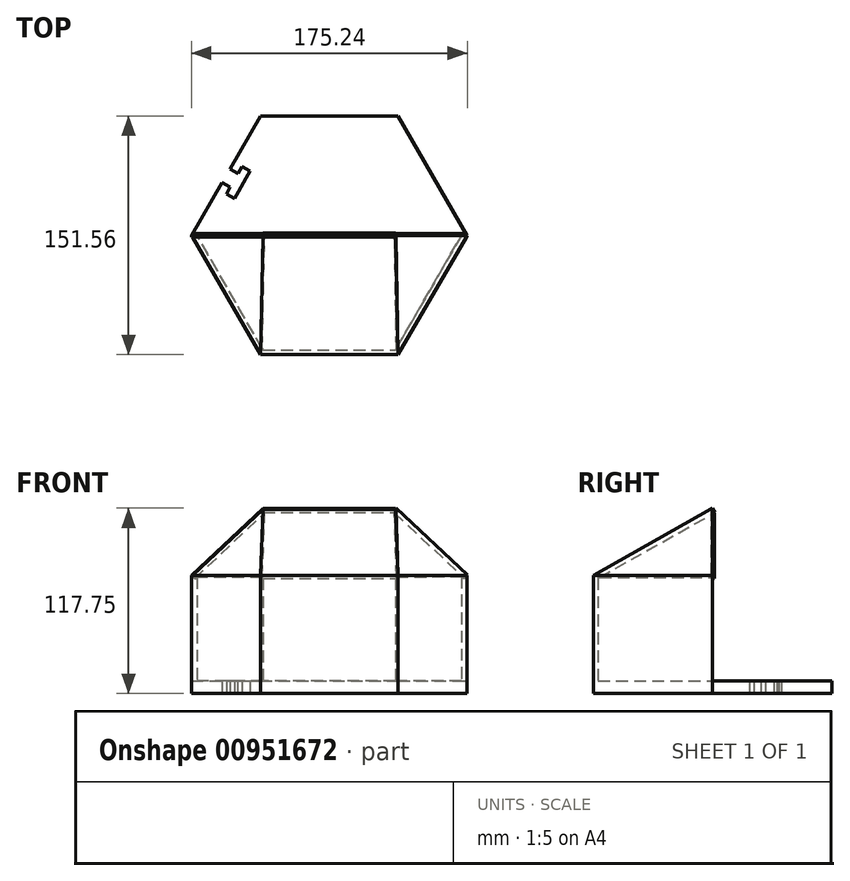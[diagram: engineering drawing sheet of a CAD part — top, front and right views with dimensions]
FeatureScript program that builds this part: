
annotation { "Feature Type Name" : "Feature", "Feature Type Description" : "" }
export const myFeature = defineFeature(function(context is Context, id is Id, definition is map)
    precondition{}
    {
        {
            var Q0;
            Q0=qCreatedBy(makeId("Top.planeOp"),FACE);
            var sketch = newSketch(context, id + "F0", { "sketchPlane" : qUnion([Q0])});
            skCircle(sketch, "E0.cCircle", {"center": v(0, 0) * mm, "radius": 75.78 * mm, "construction": true});
            skLineSegment(sketch, "E0.0", {"start": v(-43.75, 75.78) * mm, "end": v(43.75, 75.78) * mm});
            skLineSegment(sketch, "E0.1", {"start": v(43.75, 75.78) * mm, "end": v(87.5, 0) * mm});
            skLineSegment(sketch, "E0.2", {"start": v(87.5, 0) * mm, "end": v(43.75, -75.78) * mm});
            skLineSegment(sketch, "E0.3", {"start": v(43.75, -75.78) * mm, "end": v(-43.75, -75.78) * mm});
            skLineSegment(sketch, "E0.4", {"start": v(-43.75, -75.78) * mm, "end": v(-87.5, 0) * mm});
            skLineSegment(sketch, "E0.5", {"start": v(-87.5, 0) * mm, "end": v(-43.75, 75.78) * mm});
            skPoint(sketch, "E0.0.midPoint", {"position": v(0, 75.78) * mm});
            skLineSegment(sketch, "E1.0", {"start": v(-84.04, 0) * mm, "end": v(-42.02, 72.78) * mm});
            skLineSegment(sketch, "E1.1", {"start": v(42.02, 72.78) * mm, "end": v(84.04, 0) * mm});
            skLineSegment(sketch, "E1.2", {"start": v(84.04, 0) * mm, "end": v(42.02, -72.78) * mm});
            skLineSegment(sketch, "E1.3", {"start": v(-42.02, 72.78) * mm, "end": v(42.02, 72.78) * mm});
            skLineSegment(sketch, "E1.4", {"start": v(42.02, -72.78) * mm, "end": v(-42.02, -72.78) * mm});
            skLineSegment(sketch, "E1.5", {"start": v(-42.02, -72.78) * mm, "end": v(-84.04, 0) * mm});
            skLineSegment(sketch, "E2", {"start": v(-87.5, 0) * mm, "end": v(-84.04, 0) * mm});
            skLineSegment(sketch, "E3", {"start": v(84.04, 0) * mm, "end": v(87.5, 0) * mm});
            skLineSegment(sketch, "E4", {"start": v(0, 0) * mm, "end": v(0, 72.78) * mm, "construction": true});
            skLineSegment(sketch, "E5", {"start": v(0, 0) * mm, "end": v(42.02, 72.78) * mm, "construction": true});
            skLineSegment(sketch, "E6", {"start": v(0, 0) * mm, "end": v(-42.02, 72.78) * mm, "construction": true});
            skLineSegment(sketch, "E7", {"start": v(0, 36.39) * mm, "end": v(0, 72.78) * mm, "construction": true});
            skLineSegment(sketch, "E8.bottom", {"start": v(25, 48.33) * mm, "end": v(-25, 48.33) * mm});
            skLineSegment(sketch, "E8.top", {"start": v(25, 60.83) * mm, "end": v(-25, 60.83) * mm});
            skLineSegment(sketch, "E8.left", {"start": v(25, 48.33) * mm, "end": v(25, 60.83) * mm});
            skLineSegment(sketch, "E8.right", {"start": v(-25, 48.33) * mm, "end": v(-25, 60.83) * mm});
            skPoint(sketch, "E8.middle", {"position": v(0, 54.58) * mm});
            skLineSegment(sketch, "E9", {"start": v(-65.63, 37.89) * mm, "end": v(-55.16, 32) * mm, "construction": true});
            skLineSegment(sketch, "E10", {"start": v(-55.16, 32) * mm, "end": v(-52.71, 36.37) * mm, "construction": true});
            skLineSegment(sketch, "E11", {"start": v(-55.16, 32) * mm, "end": v(-57.62, 27.65) * mm, "construction": true});
            skLineSegment(sketch, "E12", {"start": v(-52.71, 36.37) * mm, "end": v(-63.12, 42.22) * mm});
            skLineSegment(sketch, "E13", {"start": v(-57.62, 27.65) * mm, "end": v(-52.71, 36.37) * mm});
            skLineSegment(sketch, "E14", {"start": v(-65.63, 37.89) * mm, "end": v(-68.13, 33.56) * mm});
            skLineSegment(sketch, "E15", {"start": v(-57.62, 27.65) * mm, "end": v(-68.13, 33.56) * mm});
            skLineSegment(sketch, "E16.MirrorCS", {"start": v(87.5, 0) * mm, "end": v(43.75, 75.78) * mm});
            skLineSegment(sketch, "E17", {"start": v(-62.87, 30.6) * mm, "end": v(-65.32, 26.25) * mm});
            skLineSegment(sketch, "E18", {"start": v(-57.62, 27.65) * mm, "end": v(-60.07, 23.3) * mm});
            skLineSegment(sketch, "E19", {"start": v(-65.32, 26.25) * mm, "end": v(-60.07, 23.3) * mm});
            skLineSegment(sketch, "E20.MirrorCS", {"start": v(-52.71, 36.37) * mm, "end": v(-50.26, 40.72) * mm});
            skLineSegment(sketch, "E21.MirrorCS", {"start": v(-57.97, 39.32) * mm, "end": v(-55.52, 43.68) * mm});
            skLineSegment(sketch, "E22.MirrorCS", {"start": v(-55.52, 43.68) * mm, "end": v(-50.26, 40.72) * mm});
            skLineSegment(sketch, "E23", {"start": v(-68.13, 33.56) * mm, "end": v(-65.5, 32.09) * mm});
            skSolve(sketch);
        }
        {
            var Q0;
            Q0=makeQuery(id+"F0.imprint","IMPRINT",FACE,{"disambiguationData":[TD([[makeQuery(id+"F0.imprint","IMPRINT",EDGE,{"derivedFrom":sQuery(id+"F0.wireOp",EDGE,"E1.0")}),-1.0]])]});
            extrude(context, id + "F1", {"entities" : qUnion([Q0]), "depth" : 8 * mm, "offsetDistance" : 25 * mm});
        }
        {
            var Q0;
            Q0=makeQuery(id+"F0.imprint","IMPRINT",FACE,{"disambiguationData":[TD([[makeQuery(id+"F0.imprint","IMPRINT",EDGE,{"derivedFrom":sQuery(id+"F0.wireOp",EDGE,"E0.2")}),-1.0]])]});
            extrude(context, id + "F2", {"entities" : qUnion([Q0]), "operationType" : NewBodyOperationType.ADD, "depth" : 75 * mm, "offsetDistance" : 25 * mm});
        }
        {
            var Q0;
            Q0=qCreatedBy(makeId("Front.planeOp"),FACE);
            var sketch = newSketch(context, id + "F3", { "sketchPlane" : qUnion([Q0])});
            skLineSegment(sketch, "E24", {"start": v(0, 0) * mm, "end": v(0, 144.27) * mm, "construction": true});
            skLineSegment(sketch, "E25", {"start": v(0, 144.27) * mm, "end": v(-94, 144.27) * mm, "construction": true});
            skLineSegment(sketch, "E26", {"start": v(0, 144.27) * mm, "end": v(81.74, 144.27) * mm});
            skLineSegment(sketch, "E27", {"start": v(0, 0) * mm, "end": v(0, 75) * mm, "construction": true});
            skLineSegment(sketch, "E28", {"start": v(0, 75) * mm, "end": v(0, 114.5) * mm, "construction": true});
            skLineSegment(sketch, "E29", {"start": v(0, 75) * mm, "end": v(-87.5, 75) * mm, "construction": true});
            skLineSegment(sketch, "E30", {"start": v(0, 114.5) * mm, "end": v(42.02, 114.5) * mm, "construction": true});
            skLineSegment(sketch, "E31", {"start": v(0, 114.5) * mm, "end": v(-42.02, 114.5) * mm});
            skLineSegment(sketch, "E32", {"start": v(0, 75) * mm, "end": v(-84.04, 75) * mm, "construction": true});
            skLineSegment(sketch, "E33", {"start": v(-42.02, 114.5) * mm, "end": v(-84.04, 75) * mm});
            skLineSegment(sketch, "E34", {"start": v(-42.02, 114.5) * mm, "end": v(-42.02, 117.5) * mm, "construction": true});
            skLineSegment(sketch, "E35", {"start": v(-42.02, 117.5) * mm, "end": v(-87.5, 75) * mm});
            skLineSegment(sketch, "E36", {"start": v(-42.02, 117.5) * mm, "end": v(0, 117.5) * mm});
            skLineSegment(sketch, "E37.MirrorCS", {"start": v(42.02, 117.5) * mm, "end": v(87.5, 75) * mm});
            skLineSegment(sketch, "E38.MirrorCS", {"start": v(42.02, 114.5) * mm, "end": v(84.04, 75) * mm});
            skLineSegment(sketch, "E39.MirrorCS", {"start": v(42.02, 117.5) * mm, "end": v(0, 117.5) * mm});
            skLineSegment(sketch, "E40.MirrorCS", {"start": v(0, 114.5) * mm, "end": v(42.02, 114.5) * mm});
            skLineSegment(sketch, "E41", {"start": v(87.5, 75) * mm, "end": v(84.04, 75) * mm});
            skLineSegment(sketch, "E42", {"start": v(-84.04, 75) * mm, "end": v(-87.5, 75) * mm});
            skSolve(sketch);
        }
        {
            var Q0;
            Q0=makeQuery(id+"F0.imprint","IMPRINT",FACE,{"disambiguationData":[TD([[makeQuery(id+"F0.imprint","IMPRINT",EDGE,{"derivedFrom":sQuery(id+"F0.wireOp",EDGE,"E0.0")}),-1.0]])]});
            extrude(context, id + "F4", {"entities" : qUnion([Q0]), "operationType" : NewBodyOperationType.ADD, "oppositeDirection" : true, "depth" : -8 * mm, "offsetDistance" : 25 * mm});
        }
        {
            var Q0;
            Q0=makeQuery(id+"F2.opExtrude","CAP_EDGE",EDGE,{"disambiguationData":[OSD([sQuery(id+"F0.wireOp",EDGE,"E0.3")])],"isStart":false});
            var Q1;
            Q1=sQuery(id+"F3.wireOp",VERTEX,"E36.end");
            cPlane(context, id + "F5", {"entities" : qUnion([Q0, Q1]), "cplaneType" : CPlaneType.LINE_ANGLE, "offset" : 25 * mm, "angle" : 0 * degree, "width" : 150 * mm, "height" : 150 * mm});
        }
        {
            var Q0;
            Q0=qCreatedBy(id+"F5.planeOp",FACE);
            var sketch = newSketch(context, id + "F6", { "sketchPlane" : qUnion([Q0])});
            skLineSegment(sketch, "E43", {"start": v(0, 29.4) * mm, "end": v(43.75, 29.4) * mm});
            skLineSegment(sketch, "E44", {"start": v(0, 29.4) * mm, "end": v(-43.75, 29.4) * mm});
            skLineSegment(sketch, "E45", {"start": v(-43.75, 29.4) * mm, "end": v(-42.02, -57.48) * mm});
            skLineSegment(sketch, "E46", {"start": v(43.75, 29.4) * mm, "end": v(42.02, -57.48) * mm});
            skLineSegment(sketch, "E47", {"start": v(-42.02, -57.48) * mm, "end": v(42.02, -57.48) * mm});
            skSolve(sketch);
        }
        {
            var Q0;
            Q0=makeQuery(id+"F6.imprint","IMPRINT",FACE,{"disambiguationData":[TD([[makeQuery(id+"F6.imprint","IMPRINT",EDGE,{"derivedFrom":sQuery(id+"F6.wireOp",EDGE,"E43")}),-1.0]])]});
            extrude(context, id + "F7", {"entities" : qUnion([Q0]), "operationType" : NewBodyOperationType.ADD, "depth" : 3 * mm, "offsetDistance" : 25 * mm});
        }
        {
            var Q0;
            Q0=makeQuery(id+"F3.imprint","IMPRINT",FACE,{"disambiguationData":[TD([[makeQuery(id+"F3.imprint","IMPRINT",EDGE,{"derivedFrom":sQuery(id+"F3.wireOp",EDGE,"E31")}),-1.0]])]});
            extrude(context, id + "F8", {"entities" : qUnion([Q0]), "operationType" : NewBodyOperationType.ADD, "depth" : 1 * mm, "offsetDistance" : 25 * mm});
        }
        {
            var Q0;
            Q0=makeQuery(id+"F8.opExtrude","CAP_EDGE",EDGE,{"disambiguationData":[OSD([sQuery(id+"F3.wireOp",EDGE,"E35")])],"isStart":true});
            var Q1;
            Q1=makeQuery(id+"F7.boolean.opBoolean","MERGE",VERTEX,{"derivedFrom":[makeQuery(id+"F2.opExtrude","CAP_VERTEX",VERTEX,{"disambiguationData":[OSD([sQuery(id+"F0.wireOp",EDGE,"E0.3"),sQuery(id+"F0.wireOp",EDGE,"E0.4")])],"isStart":false}),makeQuery(id+"F7.opExtrude","CAP_VERTEX",VERTEX,{"disambiguationData":[OSD([sQuery(id+"F6.wireOp",EDGE,"E44"),sQuery(id+"F6.wireOp",EDGE,"E45")])],"isStart":true})]});
            cPlane(context, id + "F9", {"entities" : qUnion([Q0, Q1]), "cplaneType" : CPlaneType.LINE_ANGLE, "offset" : 25 * mm, "angle" : 0 * degree, "width" : 150 * mm, "height" : 150 * mm});
        }
        {
            var Q0;
            Q0=qCreatedBy(id+"F9.planeOp",FACE);
            var sketch = newSketch(context, id + "F10", { "sketchPlane" : qUnion([Q0])});
            skLineSegment(sketch, "E48", {"start": v(-25.66, 35.61) * mm, "end": v(30.99, -31.08) * mm});
            skLineSegment(sketch, "E49", {"start": v(-25.66, 35.61) * mm, "end": v(33.23, 55.79) * mm});
            skLineSegment(sketch, "E50", {"start": v(33.23, 55.79) * mm, "end": v(30.99, -31.08) * mm});
            skSolve(sketch);
        }
        {
            var Q0;
            Q0=qSketchRegion(id+"F10",true);
            extrude(context, id + "F11", {"entities" : qUnion([Q0]), "operationType" : NewBodyOperationType.ADD, "depth" : -3 * mm, "offsetDistance" : 25 * mm});
        }
        {
            var Q0;
            Q0=makeQuery(id+"F8.opExtrude","CAP_EDGE",EDGE,{"disambiguationData":[OSD([sQuery(id+"F3.wireOp",EDGE,"E37.MirrorCS")])],"isStart":false});
            var Q1;
            Q1=makeQuery(id+"F7.boolean.opBoolean","MERGE",VERTEX,{"derivedFrom":[makeQuery(id+"F2.opExtrude","CAP_VERTEX",VERTEX,{"disambiguationData":[OSD([sQuery(id+"F0.wireOp",EDGE,"E0.2"),sQuery(id+"F0.wireOp",EDGE,"E0.3")])],"isStart":false}),makeQuery(id+"F7.opExtrude","CAP_VERTEX",VERTEX,{"disambiguationData":[OSD([sQuery(id+"F6.wireOp",EDGE,"E43"),sQuery(id+"F6.wireOp",EDGE,"E46")])],"isStart":true})]});
            cPlane(context, id + "F12", {"entities" : qUnion([Q0, Q1]), "cplaneType" : CPlaneType.LINE_ANGLE, "offset" : 25 * mm, "angle" : 0 * degree, "width" : 150 * mm, "height" : 150 * mm});
        }
        {
            var Q0;
            Q0=qCreatedBy(id+"F12.planeOp",FACE);
            var sketch = newSketch(context, id + "F13", { "sketchPlane" : qUnion([Q0])});
            skLineSegment(sketch, "E51", {"start": v(-32.88, -56.36) * mm, "end": v(25.94, -35.98) * mm});
            skLineSegment(sketch, "E52", {"start": v(25.94, -35.98) * mm, "end": v(-30.94, 30.51) * mm});
            skLineSegment(sketch, "E53", {"start": v(-30.94, 30.51) * mm, "end": v(-32.88, -56.36) * mm});
            skSolve(sketch);
        }
        {
            var Q0;
            Q0=qSketchRegion(id+"F13",true);
            extrude(context, id + "F14", {"entities" : qUnion([Q0]), "operationType" : NewBodyOperationType.ADD, "depth" : 3 * mm, "offsetDistance" : 25 * mm});
        }
        {
            var Q0;
            Q0=makeQuery(id+"F0.imprint","IMPRINT",FACE,{"disambiguationData":[TD([[makeQuery(id+"F0.imprint","IMPRINT",EDGE,{"derivedFrom":sQuery(id+"F0.wireOp",EDGE,"E8.bottom")}),-1.0]])]});
            extrude(context, id + "F15", {"entities" : qUnion([Q0]), "operationType" : NewBodyOperationType.ADD, "depth" : 8 * mm, "offsetDistance" : 25 * mm});
        }
        {
            var Q0;
            {var subQ5=sQuery(id+"F0.wireOp",EDGE,"E13");Q0=makeQuery(id+"F0.imprint","IMPRINT",FACE,{"disambiguationData":[TD([[makeQuery(id+"F0.imprint","IMPRINT",EDGE,{"derivedFrom":subQ5}),1.0]])]});}
            var Q1;
            {var subQ5=sQuery(id+"F0.wireOp",EDGE,"ALQEQqr1-oKlR-f4O9-fg5D-6GHPOLekQC52");Q1=makeQuery(id+"F0.imprint","IMPRINT",FACE,{"disambiguationData":[TD([[makeQuery(id+"F0.imprint","IMPRINT",EDGE,{"derivedFrom":subQ5}),-1.0]])]});}
            extrude(context, id + "F16", {"entities" : qUnion([Q0, Q1]), "operationType" : NewBodyOperationType.REMOVE, "oppositeDirection" : true, "depth" : 25 * mm, "offsetDistance" : 25 * mm});
        }
        {
            var Q0;
            {var subQ0=sQuery(id+"F0.wireOp",EDGE,"E2");Q0=makeQuery(id+"F0.imprint","IMPRINT",FACE,{"disambiguationData":[TD([[makeQuery(id+"F0.imprint","IMPRINT",EDGE,{"derivedFrom":subQ0}),1.0]])]});}
            extrude(context, id + "F17", {"entities" : qUnion([Q0]), "operationType" : NewBodyOperationType.ADD, "depth" : 8 * mm, "offsetDistance" : 25 * mm});
        }
    });
